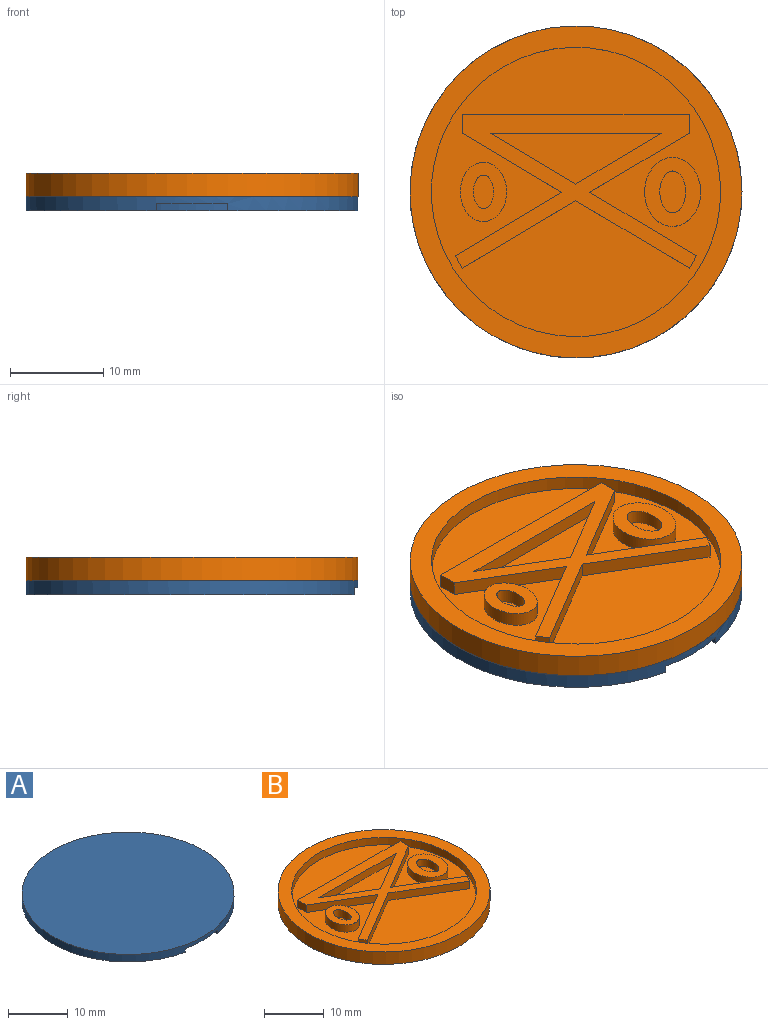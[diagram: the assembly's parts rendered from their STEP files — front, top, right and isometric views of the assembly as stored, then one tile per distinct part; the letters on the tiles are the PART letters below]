
ASSEMBLY  parts=2 mates=1
PART A: 170 faces, bbox 35.6x35.6x1.5 mm
  f0: plane 30.99x30.99mm, normal (0,0,-1), area 549.6mm2, adj f4,f5,f6,f7,f8,f9,f10,f11
  f1: plane 35.56x35.15mm, normal (0,0,-1), area 175mm2, adj f2,f165,f167,f169
  f2: cylinder r=17.78mm len=35.56mm, axis (0,0,-1), area 164.4mm2, adj f1,f3,f165,f167,f168
  f3: plane 35.56x35.56mm, normal (0,0,1), area 993.1mm2, adj f2
  f4: plane 1.49x0.76mm, normal (0,-1,0), area 1.1mm2, adj f0,f5,f15,f16
  f5: plane 7.05x0.76mm, normal (-1,0,0), area 5.4mm2, adj f0,f4,f6,f16
  f6: plane 1.49x0.76mm, normal (0,1,0), area 1.1mm2, adj f0,f5,f7,f16
  f7: plane 2.76x0.76mm, normal (1,0,0), area 2.1mm2, adj f0,f6,f8,f16
  f8: plane 2.79x0.76mm, normal (0,1,0), area 2.1mm2, adj f0,f7,f9,f16
  f9: plane 2.76x0.76mm, normal (-1,0,0), area 2.1mm2, adj f0,f8,f10,f16
  f10: plane 1.5x0.76mm, normal (0,1,0), area 1.1mm2, adj f0,f9,f11,f16
  f11: plane 7.05x0.76mm, normal (1,0,0), area 5.4mm2, adj f0,f10,f12,f16
  f12: plane 1.5x0.76mm, normal (0,-1,0), area 1.1mm2, adj f0,f11,f13,f16
  f13: plane 3.04x0.76mm, normal (-1,0,0), area 2.3mm2, adj f0,f12,f14,f16
  f14: plane 2.79x0.76mm, normal (0,-1,0), area 2.1mm2, adj f0,f13,f15,f16
  f15: plane 3.04x0.76mm, normal (1,0,0), area 2.3mm2, adj f0,f4,f14,f16
  f16: plane 7.05x5.78mm, normal (0,0,-1), area 24.5mm2, adj f4,f5,f6,f7,f8,f9,f10,f11
  f17: plane 7.05x0.76mm, normal (-1,0,0), area 5.4mm2, adj f0,f18,f41,f42
  f18: plane 2.19x0.76mm, normal (0,1,0), area 1.7mm2, adj f0,f17,f19,f42
  f19: extruded ~2.18x0.76mm, area 1.7mm2, adj f0,f18,f20,f42
  f20: extruded ~1.36x0.76mm, area 1.2mm2, adj f0,f19,f21,f42
  f21: extruded ~1.04x0.76mm, area 0.8mm2, adj f0,f20,f22,f42
  f22: extruded ~0.79x0.76mm, area 0.7mm2, adj f0,f21,f23,f42
  f23: plane 0.76x0.05mm, normal (1,0,0), area 0mm2, adj f0,f22,f24,f42
  f24: extruded ~0.97x0.76mm, area 0.9mm2, adj f0,f23,f25,f42
  f25: extruded ~1.09x0.76mm, area 0.9mm2, adj f0,f24,f26,f42
  f26: extruded ~1.51x0.76mm, area 1.3mm2, adj f0,f25,f27,f42
  f27: extruded ~1.89x0.76mm, area 1.5mm2, adj f0,f26,f41,f42
  f28: plane 0.93x0.76mm, normal (0,-1,0), area 0.7mm2, adj f29,f39,f42,f44
  f29: plane 1.84x0.76mm, normal (1,0,0), area 1.4mm2, adj f28,f30,f42,f44
  f30: plane 0.97x0.76mm, normal (0,1,0), area 0.7mm2, adj f29,f31,f42,f44
  f31: extruded ~0.91x0.76mm, area 0.7mm2, adj f30,f32,f42,f44
  f32: extruded ~0.76x0.72mm, area 0.6mm2, adj f31,f39,f42,f44
  f33: plane 1.57x0.76mm, normal (1,0,0), area 1.2mm2, adj f34,f40,f42,f43
  f34: plane 0.87x0.76mm, normal (0,1,0), area 0.7mm2, adj f33,f35,f42,f43
  f35: extruded ~0.88x0.76mm, area 0.7mm2, adj f34,f36,f42,f43
  f36: extruded ~0.76x0.62mm, area 0.5mm2, adj f35,f37,f42,f43
  f37: extruded ~0.76x0.58mm, area 0.5mm2, adj f36,f38,f42,f43
  f38: extruded ~0.94x0.76mm, area 0.7mm2, adj f37,f40,f42,f43
  f39: extruded ~1.25x0.88mm, area 1.3mm2, adj f28,f32,f42,f44
  f40: plane 0.79x0.76mm, normal (0,-1,0), area 0.6mm2, adj f33,f38,f42,f43
  f41: plane 2.64x0.76mm, normal (0,-1,0), area 2mm2, adj f0,f17,f27,f42
  f42: plane 7.05x5.23mm, normal (0,0,-1), area 27.1mm2, adj f17,f18,f19,f20,f21,f22,f23,f24
  f43: plane 2.02x1.57mm, normal (0,0,-1), area 2.9mm2, adj f33,f34,f35,f36,f37,f38,f40
  f44: plane 2.18x1.84mm, normal (0,0,-1), area 3.6mm2, adj f28,f29,f30,f31,f32,f39
  f45: extruded ~2.44x2.09mm, area 2.8mm2, adj f0,f46,f52,f53
  f46: extruded ~2.44x2.09mm, area 2.8mm2, adj f0,f45,f47,f53
  f47: extruded ~2.41x2.09mm, area 2.7mm2, adj f0,f46,f52,f53
  f48: extruded ~1.63x1.14mm, area 1.7mm2, adj f49,f51,f53,f54
  f49: extruded ~1.63x1.14mm, area 1.7mm2, adj f48,f50,f53,f54
  f50: extruded ~1.6x1.14mm, area 1.7mm2, adj f49,f51,f53,f54
  f51: extruded ~1.6x1.14mm, area 1.7mm2, adj f48,f50,f53,f54
  f52: extruded ~2.41x2.09mm, area 2.7mm2, adj f0,f45,f47,f53
  f53: plane 4.85x4.18mm, normal (0,0,-1), area 10.4mm2, adj f45,f46,f47,f48,f49,f50,f51,f52
  f54: plane 3.24x2.27mm, normal (0,0,-1), area 6mm2, adj f48,f49,f50,f51
  f55: extruded ~1.45x0.82mm, area 1.3mm2, adj f0,f56,f62,f63
  f56: extruded ~1.6x1.45mm, area 1.9mm2, adj f0,f55,f57,f63
  f57: plane 3.16x0.76mm, normal (-1,0,0), area 2.4mm2, adj f0,f56,f58,f63
  f58: plane 0.93x0.76mm, normal (0,1,0), area 0.7mm2, adj f0,f57,f59,f63
  f59: plane 3.09x0.76mm, normal (1,0,0), area 2.4mm2, adj f0,f58,f60,f63
  f60: extruded ~0.86x0.76mm, area 0.9mm2, adj f0,f59,f61,f63
  f61: extruded ~0.76x0.69mm, area 0.7mm2, adj f0,f60,f62,f63
  f62: plane 0.76x0.64mm, normal (0.59,0.81,0), area 0.6mm2, adj f0,f55,f61,f63
  f63: plane 4.76x2.9mm, normal (0,0,-1), area 5.6mm2, adj f55,f56,f57,f58,f59,f60,f61,f62
  f64: extruded ~2.19x1.82mm, area 2.5mm2, adj f0,f65,f73,f74
  f65: extruded ~2.19x1.81mm, area 2.5mm2, adj f0,f64,f66,f74
  f66: plane 2.57x0.76mm, normal (-1,0,0), area 2mm2, adj f0,f65,f67,f74
  f67: plane 0.9x0.76mm, normal (0,1,0), area 0.7mm2, adj f0,f66,f68,f74
  f68: plane 2.65x0.76mm, normal (1,0,0), area 2mm2, adj f0,f67,f69,f74
  f69: extruded ~1.3x0.91mm, area 1.4mm2, adj f0,f68,f70,f74
  f70: extruded ~1.3x0.88mm, area 1.4mm2, adj f0,f69,f71,f74
  f71: plane 2.65x0.76mm, normal (-1,0,0), area 2mm2, adj f0,f70,f72,f74
  f72: plane 0.93x0.76mm, normal (0,1,0), area 0.7mm2, adj f0,f71,f73,f74
  f73: plane 2.57x0.76mm, normal (1,0,0), area 2mm2, adj f0,f64,f72,f74
  f74: plane 4.76x3.62mm, normal (0,0,-1), area 9.2mm2, adj f64,f65,f66,f67,f68,f69,f70,f71
  f75: plane 4.67x0.76mm, normal (1,0,0), area 3.6mm2, adj f0,f76,f90,f91
  f76: plane 0.88x0.76mm, normal (0,-1,0), area 0.7mm2, adj f0,f75,f77,f91
  f77: plane 1.88x0.76mm, normal (-1,0,0), area 1.4mm2, adj f0,f76,f78,f91
  f78: extruded ~1.63x0.76mm, area 1.2mm2, adj f0,f77,f79,f91
  f79: plane 0.76x0.03mm, normal (0,-1,0), area 0mm2, adj f0,f78,f80,f91
  f80: plane 1x0.76mm, normal (0.9,-0.43,0), area 0.8mm2, adj f0,f79,f81,f91
  f81: plane 2.5x1.35mm, normal (0.88,-0.48,0), area 2.2mm2, adj f0,f80,f82,f91
  f82: plane 0.95x0.76mm, normal (0,-1,0), area 0.7mm2, adj f0,f81,f83,f91
  f83: plane 4.67x0.76mm, normal (-1,0,0), area 3.6mm2, adj f0,f82,f84,f91
  f84: plane 0.88x0.76mm, normal (0,1,0), area 0.7mm2, adj f0,f83,f85,f91
  f85: plane 1.86x0.76mm, normal (1,0,0), area 1.4mm2, adj f0,f84,f86,f91
  f86: extruded ~1.64x0.76mm, area 1.3mm2, adj f0,f85,f87,f91
  f87: plane 0.76x0.03mm, normal (0,1,0), area 0mm2, adj f0,f86,f88,f91
  f88: plane 1.01x0.76mm, normal (-0.91,0.42,0), area 0.8mm2, adj f0,f87,f89,f91
  f89: plane 2.49x1.36mm, normal (-0.88,0.48,0), area 2.2mm2, adj f0,f88,f90,f91
  f90: plane 0.95x0.76mm, normal (0,1,0), area 0.7mm2, adj f0,f75,f89,f91
  f91: plane 4.67x3.57mm, normal (0,0,-1), area 10.9mm2, adj f75,f76,f77,f78,f79,f80,f81,f82
  f92: plane 2.41x1.31mm, normal (0.88,0.48,0), area 2.1mm2, adj f0,f93,f109,f110
  f93: plane 0.99x0.76mm, normal (0,-1,0), area 0.8mm2, adj f0,f92,f94,f110
  f94: plane 1.04x0.76mm, normal (-0.9,-0.43,0), area 0.9mm2, adj f0,f93,f95,f110
  f95: extruded ~0.77x0.76mm, area 0.6mm2, adj f0,f94,f96,f110
  f96: plane 0.76x0.02mm, normal (0,-1,0), area 0mm2, adj f0,f95,f97,f110
  f97: extruded ~0.77x0.76mm, area 0.6mm2, adj f0,f96,f98,f110
  f98: plane 1.04x0.76mm, normal (0.89,-0.45,0), area 0.9mm2, adj f0,f97,f99,f110
  f99: plane 1.04x0.76mm, normal (0,-1,0), area 0.8mm2, adj f0,f98,f100,f110
  f100: plane 2.37x1.31mm, normal (-0.87,0.48,0), area 2.1mm2, adj f0,f99,f101,f110
  f101: plane 2.3x1.23mm, normal (-0.88,-0.47,0), area 2mm2, adj f0,f100,f102,f110
  f102: plane 0.98x0.76mm, normal (0,1,0), area 0.8mm2, adj f0,f101,f103,f110
  f103: plane 0.96x0.76mm, normal (0.91,0.42,0), area 0.8mm2, adj f0,f102,f104,f110
  f104: extruded ~0.76x0.74mm, area 0.6mm2, adj f0,f103,f105,f110
  f105: plane 0.76x0.03mm, normal (0,1,0), area 0mm2, adj f0,f104,f106,f110
  f106: extruded ~0.76x0.74mm, area 0.6mm2, adj f0,f105,f107,f110
  f107: plane 0.96x0.76mm, normal (-0.9,0.44,0), area 0.8mm2, adj f0,f106,f108,f110
  f108: plane 1.04x0.76mm, normal (0,1,0), area 0.8mm2, adj f0,f107,f109,f110
  f109: plane 2.26x1.23mm, normal (0.88,-0.48,0), area 2mm2, adj f0,f92,f108,f110
  f110: plane 4.67x3.78mm, normal (0,0,-1), area 8.4mm2, adj f92,f93,f94,f95,f96,f97,f98,f99
  f111: plane 4.67x0.76mm, normal (1,0,0), area 3.6mm2, adj f0,f112,f114,f115
  f112: plane 0.94x0.76mm, normal (0,-1,0), area 0.7mm2, adj f0,f111,f113,f115
  f113: plane 4.67x0.76mm, normal (-1,0,0), area 3.6mm2, adj f0,f112,f114,f115
  f114: plane 0.94x0.76mm, normal (0,1,0), area 0.7mm2, adj f0,f111,f113,f115
  f115: plane 4.67x0.94mm, normal (0,0,-1), area 4.4mm2, adj f111,f112,f113,f114
  f116: plane 4.67x0.76mm, normal (1,0,0), area 3.6mm2, adj f0,f117,f131,f132
  f117: plane 0.88x0.76mm, normal (0,-1,0), area 0.7mm2, adj f0,f116,f118,f132
  f118: plane 1.88x0.76mm, normal (-1,0,0), area 1.4mm2, adj f0,f117,f119,f132
  f119: extruded ~1.63x0.76mm, area 1.2mm2, adj f0,f118,f120,f132
  f120: plane 0.76x0.03mm, normal (0,-1,0), area 0mm2, adj f0,f119,f121,f132
  f121: plane 1x0.76mm, normal (0.9,-0.43,0), area 0.8mm2, adj f0,f120,f122,f132
  f122: plane 2.5x1.35mm, normal (0.88,-0.48,0), area 2.2mm2, adj f0,f121,f123,f132
  f123: plane 0.95x0.76mm, normal (0,-1,0), area 0.7mm2, adj f0,f122,f124,f132
  f124: plane 4.67x0.76mm, normal (-1,0,0), area 3.6mm2, adj f0,f123,f125,f132
  f125: plane 0.88x0.76mm, normal (0,1,0), area 0.7mm2, adj f0,f124,f126,f132
  f126: plane 1.86x0.76mm, normal (1,0,0), area 1.4mm2, adj f0,f125,f127,f132
  f127: extruded ~1.64x0.76mm, area 1.3mm2, adj f0,f126,f128,f132
  f128: plane 0.76x0.03mm, normal (0,1,0), area 0mm2, adj f0,f127,f129,f132
  f129: plane 1.01x0.76mm, normal (-0.91,0.42,0), area 0.8mm2, adj f0,f128,f130,f132
  f130: plane 2.49x1.36mm, normal (-0.88,0.48,0), area 2.2mm2, adj f0,f129,f131,f132
  f131: plane 0.95x0.76mm, normal (0,1,0), area 0.7mm2, adj f0,f116,f130,f132
  f132: plane 4.67x3.57mm, normal (0,0,-1), area 10.9mm2, adj f116,f117,f118,f119,f120,f121,f122,f123
  f133: extruded ~1.78x0.76mm, area 1.4mm2, adj f134,f146,f147,f163
  f134: extruded ~1.78x0.76mm, area 1.4mm2, adj f133,f135,f147,f163
  f135: extruded ~1.35x0.76mm, area 1.2mm2, adj f134,f136,f147,f163
  f136: extruded ~2.38x1.78mm, area 2.6mm2, adj f135,f137,f147,f163
  f137: extruded ~2.38x1.79mm, area 2.6mm2, adj f136,f146,f147,f163
  f138: extruded ~2.69x0.87mm, area 2.2mm2, adj f0,f139,f145,f147
  f139: extruded ~2.69x0.86mm, area 2.2mm2, adj f0,f138,f140,f147
  f140: extruded ~2.49x0.94mm, area 2.1mm2, adj f0,f139,f141,f147
  f141: extruded ~2.5x0.93mm, area 2.1mm2, adj f0,f140,f142,f147
  f142: extruded ~2.69x0.87mm, area 2.2mm2, adj f0,f141,f143,f147
  f143: extruded ~2.7x0.87mm, area 2.2mm2, adj f0,f142,f144,f147
  f144: extruded ~2.49x0.94mm, area 2.1mm2, adj f0,f143,f145,f147
  f145: extruded ~2.49x0.94mm, area 2.1mm2, adj f0,f138,f144,f147
  f146: extruded ~1.34x0.76mm, area 1.2mm2, adj f133,f137,f147,f163
  f147: plane 7.26x6.71mm, normal (0,0,-1), area 26mm2, adj f133,f134,f135,f136,f137,f138,f139,f140
  f148: extruded ~1.78x0.76mm, area 1.4mm2, adj f149,f161,f162,f164
  f149: extruded ~1.78x0.76mm, area 1.4mm2, adj f148,f150,f162,f164
  f150: extruded ~1.35x0.76mm, area 1.2mm2, adj f149,f151,f162,f164
  f151: extruded ~2.38x1.78mm, area 2.6mm2, adj f150,f152,f162,f164
  f152: extruded ~2.38x1.79mm, area 2.6mm2, adj f151,f161,f162,f164
  f153: extruded ~2.69x0.87mm, area 2.2mm2, adj f0,f154,f160,f162
  f154: extruded ~2.69x0.86mm, area 2.2mm2, adj f0,f153,f155,f162
  f155: extruded ~2.49x0.94mm, area 2.1mm2, adj f0,f154,f156,f162
  f156: extruded ~2.5x0.93mm, area 2.1mm2, adj f0,f155,f157,f162
  f157: extruded ~2.69x0.87mm, area 2.2mm2, adj f0,f156,f158,f162
  f158: extruded ~2.7x0.87mm, area 2.2mm2, adj f0,f157,f159,f162
  f159: extruded ~2.49x0.94mm, area 2.1mm2, adj f0,f158,f160,f162
  f160: extruded ~2.49x0.94mm, area 2.1mm2, adj f0,f153,f159,f162
  f161: extruded ~1.34x0.76mm, area 1.2mm2, adj f148,f152,f162,f164
  f162: plane 7.26x6.71mm, normal (0,0,-1), area 26mm2, adj f148,f149,f150,f151,f152,f153,f154,f155
  f163: plane 4.76x3.58mm, normal (0,0,-1), area 14.2mm2, adj f133,f134,f135,f136,f137,f146
  f164: plane 4.76x3.58mm, normal (0,0,-1), area 14.2mm2, adj f148,f149,f150,f151,f152,f161
  f165: plane 1.83x0.76mm, normal (1,0,0), area 1.4mm2, adj f1,f2,f168,f169
  f166: cylinder r=15.49mm len=30.99mm, axis (0,0,-1), area 74.2mm2, adj f0,f168
  f167: plane 1.83x0.76mm, normal (-1,0,0), area 1.4mm2, adj f1,f2,f168,f169
  f168: plane 33.78x32mm, normal (0,0,-1), area 63.9mm2, adj f2,f165,f166,f167,f169
  f169: cylinder r=16mm len=32mm, axis (0,0,-1), area 70.8mm2, adj f1,f165,f167,f168
PART B: 29 faces, bbox 35.6x35.6x2.5 mm
  f0: cylinder r=17.78mm len=35.56mm, axis (0,0,-1), area 283.8mm2, adj f1,f2
  f1: plane 35.56x35.56mm, normal (0,0,1), area 239mm2, adj f0,f3
  f2: plane 35.56x35.56mm, normal (0,0,-1), area 993.1mm2, adj f0
  f3: cylinder r=15.49mm len=30.99mm, axis (0,0,1), area 148.4mm2, adj f1,f4
  f4: plane 30.99x30.99mm, normal (0,0,1), area 515.7mm2, adj f3,f8,f9,f10,f11,f12,f13,f14
  f5: plane 25.83x16.49mm, normal (0,0,1), area 128.9mm2, adj f6,f7,f8,f9,f10,f11,f12,f13
  f6: plane 9.16x5.46mm, normal (-0.51,0.86,0), area 16.2mm2, adj f5,f7,f19,f20
  f7: plane 9.16x5.46mm, normal (0.51,0.86,0), area 16.2mm2, adj f5,f6,f19,f20
  f8: plane 11.43x6.81mm, normal (0.51,0.86,0), area 20.3mm2, adj f4,f5,f9,f18
  f9: plane 10.65x6.34mm, normal (0.51,-0.86,0), area 18.9mm2, adj f4,f5,f8,f10
  f10: plane 2.03x1.52mm, normal (1,0,0), area 3.1mm2, adj f4,f5,f9,f11
  f11: plane 24.27x1.52mm, normal (0,1,0), area 37mm2, adj f4,f5,f10,f12
  f12: plane 2.03x1.52mm, normal (-1,0,0), area 3.1mm2, adj f4,f5,f11,f13
  f13: plane 10.65x6.34mm, normal (-0.51,-0.86,0), area 18.9mm2, adj f4,f5,f12,f14
  f14: plane 11.43x6.81mm, normal (-0.51,0.86,0), area 20.3mm2, adj f4,f5,f13,f15
  f15: plane 1.52x1.31mm, normal (-0.86,-0.51,0), area 2.3mm2, adj f4,f5,f14,f16
  f16: plane 12.14x7.23mm, normal (0.51,-0.86,0), area 21.5mm2, adj f4,f5,f15,f17
  f17: plane 12.14x7.23mm, normal (-0.51,-0.86,0), area 21.5mm2, adj f4,f5,f16,f18
  f18: plane 1.52x1.31mm, normal (0.86,-0.51,0), area 2.3mm2, adj f4,f5,f8,f17
  f19: plane 18.32x1.52mm, normal (0,-1,0), area 27.9mm2, adj f5,f6,f7,f20
  f20: plane 18.32x5.46mm, normal (0,0,1), area 50mm2, adj f6,f7,f19
  f21: plane 6.34x4.97mm, normal (0,0,1), area 18.6mm2, adj f22,f23
  f22: extruded ~3.59x2.18mm, area 14mm2, adj f21,f24
  f23: extruded ~6.34x4.97mm, area 27.2mm2, adj f4,f21
  f24: plane 3.59x2.18mm, normal (0,0,1), area 6.1mm2, adj f22
  f25: plane 7.38x6.01mm, normal (0,0,1), area 25.1mm2, adj f26,f27
  f26: extruded ~4.49x2.76mm, area 17.6mm2, adj f25,f28
  f27: extruded ~7.38x6.01mm, area 32.1mm2, adj f4,f25
  f28: plane 4.49x2.76mm, normal (0,0,1), area 9.7mm2, adj f26
PLACE A t=(-6.45,-25.08,-33.67)mm
PLACE B t=(-6.45,-25.08,-32.14)mm fixed
MATE fastened A.f2 <-> B.f0  axis (0,0,1) through (-6.45,-25.08,-32.14)mm
